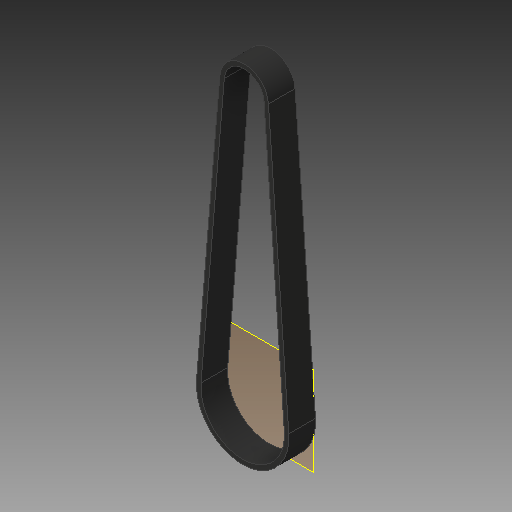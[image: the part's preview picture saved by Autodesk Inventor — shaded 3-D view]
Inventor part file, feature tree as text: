
AUTODESK INVENTOR PART (.ipt)
format: ipt  version: 2018.2 (Build 222227000, 227)  size: 122,880 bytes
history: native  units: mm
features: other x5, reference x2, plane x1, extrude x1, sketch x1
ambient origin geometry x8: Origin, YZ Plane, XZ Plane, XY Plane, X Axis, Y Axis, Z Axis, Center Point
bodies: Solid1 (feature_tree)
feature tree (10):
  plane  "Work Plane1"
  extrude  "Extrusion1"  Depth=6.0mm
  sketch  "Sketch1"  dims[d0=1.0mm d1=0.3mm d2=0.3mm d3=1.0mm d4=6.0mm d5=0.0mm]
  reference  "Reference1"
  reference  "Reference2"
  other  "ReleaseAssembly.iam"
  other  "PitchAssembly:1"
  other  "GT2Shaft32T:1"
  other  "YawAssembly:1"
  other  "GT2Yaw:1"
